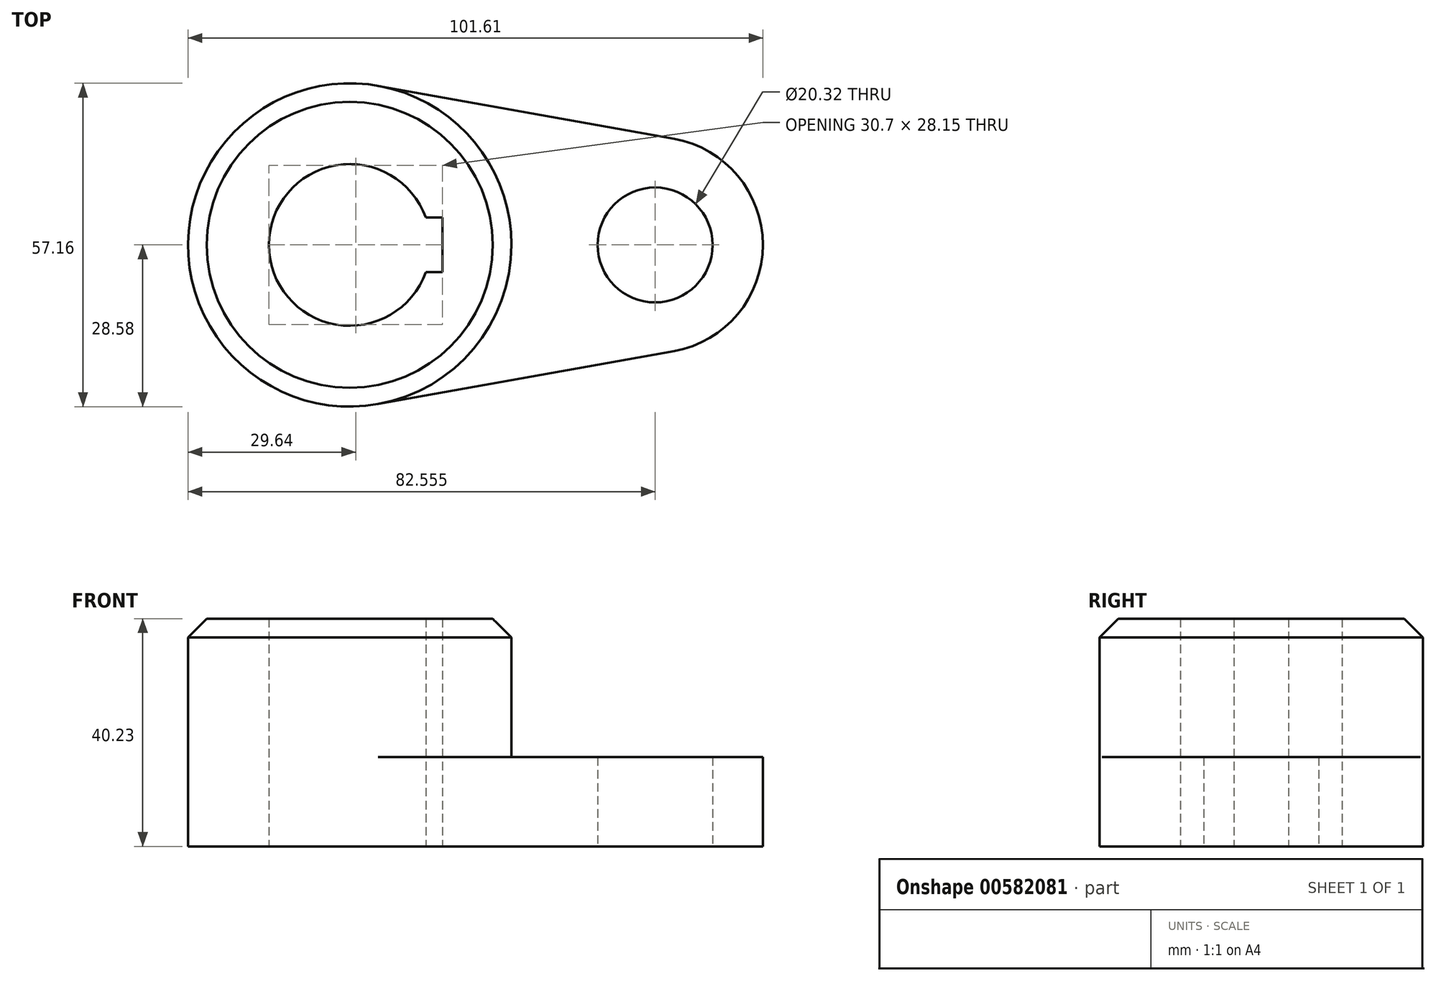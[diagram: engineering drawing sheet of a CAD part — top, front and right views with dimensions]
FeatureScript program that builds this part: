
annotation { "Feature Type Name" : "Feature", "Feature Type Description" : "" }
export const myFeature = defineFeature(function(context is Context, id is Id, definition is map)
    precondition{}
    {
        {
            var Q0;
            Q0=qCreatedBy(makeId("Top.planeOp"),FACE);
            var sketch = newSketch(context, id + "F0", { "sketchPlane" : qUnion([Q0])});
            skCircle(sketch, "E0", {"center": v(0, 0) * mm, "radius": 14.29 * mm});
            skCircle(sketch, "E1", {"center": v(0, 0) * mm, "radius": 28.58 * mm});
            skLineSegment(sketch, "E2.bottom", {"start": v(-16.4, 4.83) * mm, "end": v(16.4, 4.83) * mm});
            skLineSegment(sketch, "E2.top", {"start": v(-16.4, -4.83) * mm, "end": v(16.4, -4.83) * mm});
            skLineSegment(sketch, "E2.left", {"start": v(-16.4, 4.83) * mm, "end": v(-16.4, -4.83) * mm});
            skLineSegment(sketch, "E2.right", {"start": v(16.4, 4.83) * mm, "end": v(16.4, -4.83) * mm});
            skCircle(sketch, "E3", {"center": v(53.98, 0) * mm, "radius": 10.16 * mm});
            skCircle(sketch, "E4", {"center": v(53.98, 0) * mm, "radius": 19.05 * mm});
            skLineSegment(sketch, "E5", {"start": v(5.04, 28.13) * mm, "end": v(57.34, 18.75) * mm});
            skLineSegment(sketch, "E6", {"start": v(5.04, -28.13) * mm, "end": v(57.34, -18.75) * mm});
            skSolve(sketch);
        }
        {
            var Q0;
            Q0 = qSketchRegion(id + "F0", true);
            var Q1;
            {var subQ5=sQuery(id+"F0.wireOp",EDGE,"E2.left");Q1=makeQuery(id+"F0.imprint","IMPRINT",FACE,{"disambiguationData":[TD([[makeQuery(id+"F0.imprint","IMPRINT",EDGE,{"derivedFrom":subQ5}),1.0]])]});}
            extrude(context, id + "F1", {"entities" : qUnion([Q0, Q1]), "depth" : 15.77 * mm, "offsetDistance" : 25.4 * mm});
        }
        {
            var Q0;
            Q0=makeQuery(id+"F1.opExtrude","CAP_FACE",FACE,{"disambiguationData":[OSD([sQuery(id+"F0.wireOp",EDGE,"E0"),sQuery(id+"F0.wireOp",EDGE,"E1"),sQuery(id+"F0.wireOp",EDGE,"E2.bottom"),sQuery(id+"F0.wireOp",EDGE,"E2.top"),sQuery(id+"F0.wireOp",EDGE,"E2.left"),sQuery(id+"F0.wireOp",EDGE,"E2.right"),sQuery(id+"F0.wireOp",EDGE,"E3"),sQuery(id+"F0.wireOp",EDGE,"E4"),sQuery(id+"F0.wireOp",EDGE,"E5"),sQuery(id+"F0.wireOp",EDGE,"E6")])],"isStart":false});
            var sketch = newSketch(context, id + "F2", { "sketchPlane" : qUnion([Q0])});
            skLineSegment(sketch, "E7.0", {"start": v(13.45, -4.83) * mm, "end": v(13.45, -4.83) * mm});
            skLineSegment(sketch, "E8.0", {"start": v(13.45, 4.83) * mm, "end": v(13.45, 4.83) * mm});
            skArc(sketch, "E9.0", {"start": v(13.45, 4.83) * mm, "mid": v(-14.29, 0) * mm, "end": v(13.45, -4.83) * mm});
            skLineSegment(sketch, "E10.0", {"start": v(16.4, 4.83) * mm, "end": v(16.4, -4.83) * mm});
            skLineSegment(sketch, "E11.0", {"start": v(13.45, 4.83) * mm, "end": v(16.4, 4.83) * mm});
            skLineSegment(sketch, "E12.0", {"start": v(13.45, -4.83) * mm, "end": v(16.4, -4.83) * mm});
            skCircle(sketch, "E13.0", {"center": v(0, 0) * mm, "radius": 28.58 * mm});
            skCircle(sketch, "E14.0", {"center": v(53.98, 0) * mm, "radius": 10.16 * mm});
            skCircle(sketch, "E15.0", {"center": v(53.98, 0) * mm, "radius": 19.05 * mm});
            skSolve(sketch);
        }
        {
            var Q0;
            Q0=makeQuery(id+"F2.imprint","IMPRINT",FACE,{"disambiguationData":[TD([[makeQuery(id+"F2.imprint","IMPRINT",EDGE,{"derivedFrom":sQuery(id+"F2.wireOp",EDGE,"E10.0")}),1.0]])]});
            var Q1;
            {var subQ1=sQuery(id+"F0.wireOp",EDGE,"E2.left");Q1=makeQuery(id+"F2.imprint","IMPRINT",FACE,{"disambiguationData":[TD([[makeQuery(id+"F2.imprint","IMPRINT",EDGE,{"derivedFrom":makeQuery(id+"F1.opExtrude","CAP_EDGE",EDGE,{"disambiguationData":[OSD([subQ1])],"isStart":false})}),1.0]])]});}
            extrude(context, id + "F3", {"entities" : qUnion([Q0, Q1]), "operationType" : NewBodyOperationType.ADD, "depth" : 24.46 * mm, "offsetDistance" : 25.4 * mm});
        }
        {
            var Q0;
            Q0=makeQuery(id+"F3.opExtrude","CAP_EDGE",EDGE,{"disambiguationData":[OSD([sQuery(id+"F2.wireOp",EDGE,"E13.0")])],"isStart":false});
            chamfer(context, id + "F4", {"entities" : qUnion([Q0]), "width" : 3.3 * mm, "tangentPropagation" : true});
        }
    });
